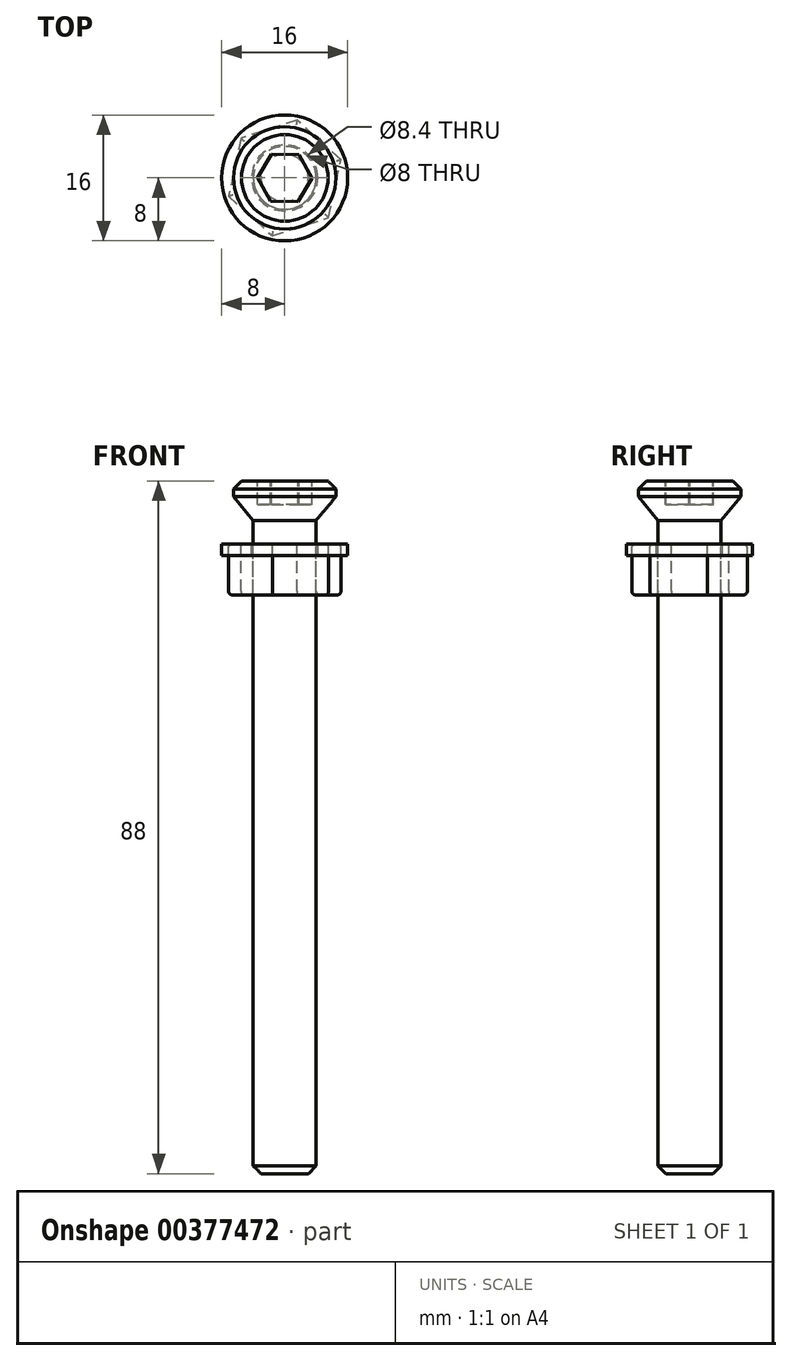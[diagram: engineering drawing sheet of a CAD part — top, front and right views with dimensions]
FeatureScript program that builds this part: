
annotation { "Feature Type Name" : "Feature", "Feature Type Description" : "" }
export const myFeature = defineFeature(function(context is Context, id is Id, definition is map)
    precondition{}
    {
        {
            var Q0;
            Q0=qCreatedBy(makeId("Top.planeOp"),FACE);
            var sketch = newSketch(context, id + "F0", { "sketchPlane" : qUnion([Q0])});
            skCircle(sketch, "E0", {"center": v(0, 0) * mm, "radius": 6.5 * mm});
            skSolve(sketch);
        }
        {
            var Q0;
            Q0 = qSketchRegion(id + "F0", true);
            extrude(context, id + "F1", {"entities" : qUnion([Q0]), "depth" : 8 * mm});
        }
        {
            var Q0;
            Q0=makeQuery(id+"F1.opExtrude","CAP_FACE",FACE,{"disambiguationData":[OSD([sQuery(id+"F0.wireOp",EDGE,"E0")])],"isStart":true});
            var sketch = newSketch(context, id + "F2", { "sketchPlane" : qUnion([Q0])});
            skCircle(sketch, "E1", {"center": v(0, 0) * mm, "radius": 4 * mm});
            skSolve(sketch);
        }
        {
            var Q0;
            Q0 = qSketchRegion(id + "F2", true);
            extrude(context, id + "F3", {"entities" : qUnion([Q0]), "operationType" : NewBodyOperationType.ADD, "depth" : 80 * mm});
        }
        {
            var Q0;
            Q0=makeQuery(id+"F1.opExtrude","CAP_FACE",FACE,{"disambiguationData":[OSD([sQuery(id+"F0.wireOp",EDGE,"E0")])],"isStart":false});
            var sketch = newSketch(context, id + "F4", { "sketchPlane" : qUnion([Q0])});
            skCircle(sketch, "E2.cCircle", {"center": v(0, 0) * mm, "radius": 3 * mm, "construction": true});
            skLineSegment(sketch, "E2.0", {"start": v(-3.46, 0.06) * mm, "end": v(-1.68, 3.03) * mm});
            skLineSegment(sketch, "E2.1", {"start": v(-1.68, 3.03) * mm, "end": v(1.78, 2.97) * mm});
            skLineSegment(sketch, "E2.2", {"start": v(1.78, 2.97) * mm, "end": v(3.46, -0.06) * mm});
            skLineSegment(sketch, "E2.3", {"start": v(3.46, -0.06) * mm, "end": v(1.68, -3.03) * mm});
            skLineSegment(sketch, "E2.4", {"start": v(1.68, -3.03) * mm, "end": v(-1.78, -2.97) * mm});
            skLineSegment(sketch, "E2.5", {"start": v(-1.78, -2.97) * mm, "end": v(-3.46, 0.06) * mm});
            skPoint(sketch, "E2.0.midPoint", {"position": v(-2.57, 1.55) * mm});
            skSolve(sketch);
        }
        {
            var Q0;
            Q0 = qSketchRegion(id + "F4", true);
            extrude(context, id + "F5", {"entities" : qUnion([Q0]), "operationType" : NewBodyOperationType.REMOVE, "oppositeDirection" : true, "depth" : 3 * mm});
        }
        {
            var Q0;
            Q0=makeQuery(id+"F3.opExtrude","CAP_EDGE",EDGE,{"disambiguationData":[OSD([sQuery(id+"F2.wireOp",EDGE,"E1")])],"isStart":false});
            var Q1;
            Q1=makeQuery(id+"F1.opExtrude","CAP_EDGE",EDGE,{"disambiguationData":[OSD([sQuery(id+"F0.wireOp",EDGE,"E0")])],"isStart":false});
            chamfer(context, id + "F6", {"entities" : qUnion([Q0, Q1]), "width" : 1 * mm, "tangentPropagation" : true});
        }
        {
            var Q0;
            Q0=makeQuery(id+"F1.opExtrude","CAP_FACE",FACE,{"disambiguationData":[OSD([sQuery(id+"F0.wireOp",EDGE,"E0")])],"isStart":true});
            var sketch = newSketch(context, id + "F7", { "sketchPlane" : qUnion([Q0])});
            skCircle(sketch, "E3.cCircle", {"center": v(0, 0) * mm, "radius": 6.5 * mm, "construction": true});
            skLineSegment(sketch, "E3.0", {"start": v(7.14, -2.3) * mm, "end": v(1.58, -7.34) * mm});
            skLineSegment(sketch, "E3.1", {"start": v(1.58, -7.34) * mm, "end": v(-5.57, -5.03) * mm});
            skLineSegment(sketch, "E3.2", {"start": v(-5.57, -5.03) * mm, "end": v(-7.14, 2.3) * mm});
            skLineSegment(sketch, "E3.3", {"start": v(-7.14, 2.3) * mm, "end": v(-1.58, 7.34) * mm});
            skLineSegment(sketch, "E3.4", {"start": v(-1.58, 7.34) * mm, "end": v(5.57, 5.03) * mm});
            skLineSegment(sketch, "E3.5", {"start": v(5.57, 5.03) * mm, "end": v(7.14, -2.3) * mm});
            skPoint(sketch, "E3.0.midPoint", {"position": v(4.36, -4.82) * mm});
            skCircle(sketch, "E4", {"center": v(0, 0) * mm, "radius": 4 * mm});
            skSolve(sketch);
        }
        {
            var Q0;
            Q0 = qSketchRegion(id + "F7", true);
            extrude(context, id + "F8", {"entities" : qUnion([Q0]), "depth" : 6.5 * mm});
        }
        {
            var Q0;
            Q0=makeQuery(id+"F8.opExtrude","CAP_FACE",FACE,{"disambiguationData":[OSD([sQuery(id+"F7.wireOp",EDGE,"E3.0"),sQuery(id+"F7.wireOp",EDGE,"E3.1"),sQuery(id+"F7.wireOp",EDGE,"E3.2"),sQuery(id+"F7.wireOp",EDGE,"E3.3"),sQuery(id+"F7.wireOp",EDGE,"E3.4"),sQuery(id+"F7.wireOp",EDGE,"E3.5")])],"isStart":false});
            var Q1;
            Q1=makeQuery(id+"F8.opExtrude","CAP_FACE",FACE,{"disambiguationData":[OSD([sQuery(id+"F7.wireOp",EDGE,"E3.0"),sQuery(id+"F7.wireOp",EDGE,"E3.1"),sQuery(id+"F7.wireOp",EDGE,"E3.2"),sQuery(id+"F7.wireOp",EDGE,"E3.3"),sQuery(id+"F7.wireOp",EDGE,"E3.4"),sQuery(id+"F7.wireOp",EDGE,"E3.5")])],"isStart":true});
            fillet(context, id + "F9", {"entities" : qUnion([Q0, Q1]), "radius" : .5 * mm, "tangentPropagation" : true, "allowEdgeOverflow" : false});
        }
        {
            var Q0;
            Q0=makeQuery(id+"F1.opExtrude","CAP_FACE",FACE,{"disambiguationData":[OSD([sQuery(id+"F0.wireOp",EDGE,"E0")])],"isStart":true});
            var sketch = newSketch(context, id + "F10", { "sketchPlane" : qUnion([Q0])});
            skCircle(sketch, "E5", {"center": v(0, 0) * mm, "radius": 8 * mm});
            skCircle(sketch, "E6", {"center": v(0, 0) * mm, "radius": 4.2 * mm});
            skSolve(sketch);
        }
        {
            var Q0;
            Q0 = qSketchRegion(id + "F10", true);
            extrude(context, id + "F11", {"entities" : qUnion([Q0]), "depth" : 1.5 * mm});
        }
        {
            var Q0;
            Q0=makeQuery(id+"F1.opExtrude","CAP_EDGE",EDGE,{"disambiguationData":[OSD([sQuery(id+"F0.wireOp",EDGE,"E0")])],"isStart":true});
            chamfer(context, id + "F12", {"entities" : qUnion([Q0]), "chamferType" : ChamferType.TWO_OFFSETS, "width1" : 6 * mm, "oppositeDirection" : false, "width2" : 5 * mm, "tangentPropagation" : true});
        }
    });
